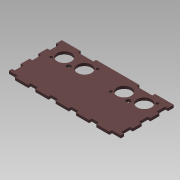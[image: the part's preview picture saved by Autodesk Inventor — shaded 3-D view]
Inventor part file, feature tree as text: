
AUTODESK INVENTOR PART (.ipt)
format: ipt  version: 2015 SP1 (Build 190203100, 203)  size: 171,008 bytes
history: native  units: mm
features: extrude x1, sketch x1
ambient origin geometry x8: Origin, YZ Plane, XZ Plane, XY Plane, X Axis, Y Axis, Z Axis, Center Point
bodies: Solid1 (feature_tree)
feature tree (2):
  extrude  "Extrusion1"  Depth=3.0mm
  sketch  "Sketch1"  dims[d0=15.0mm d1=3.0mm d3=30.0mm d5=23.0mm d6=30.0mm d8=23.0mm d11=3.0mm d12=3.0mm d13=90.0deg d14=3.0mm d17=3.0mm d18=10.0mm d20=10.0mm d21=3.0mm d22=0.0mm]
